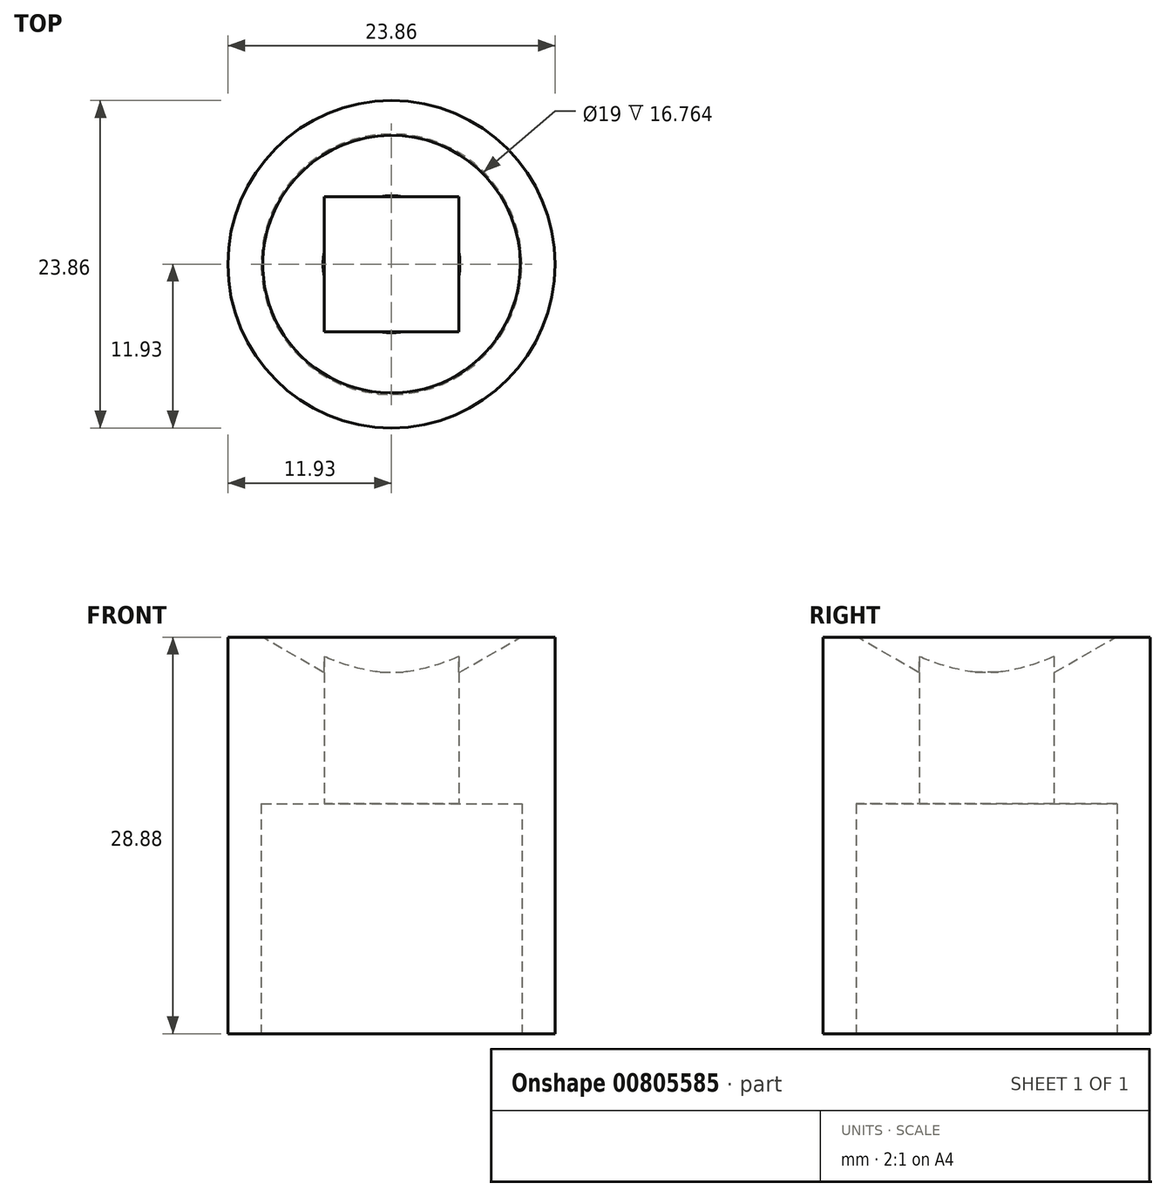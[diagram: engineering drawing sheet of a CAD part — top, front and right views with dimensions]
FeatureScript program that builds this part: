
annotation { "Feature Type Name" : "Feature", "Feature Type Description" : "" }
export const myFeature = defineFeature(function(context is Context, id is Id, definition is map)
    precondition{}
    {
        {
            var Q0;
            Q0=qCreatedBy(makeId("Top.planeOp"),FACE);
            var sketch = newSketch(context, id + "F0", { "sketchPlane" : qUnion([Q0])});
            skCircle(sketch, "E0", {"center": v(0, 0) * mm, "radius": 11.93 * mm});
            skSolve(sketch);
        }
        {
            var Q0;
            Q0 = qSketchRegion(id + "F0", true);
            extrude(context, id + "F1", {"entities" : qUnion([Q0]), "depth" : 28.88 * mm, "offsetDistance" : 25.4 * mm});
        }
        {
            var Q0;
            Q0=makeQuery(id+"F1.opExtrude","CAP_FACE",FACE,{"disambiguationData":[OSD([sQuery(id+"F0.wireOp",EDGE,"E0")])],"isStart":false});
            var sketch = newSketch(context, id + "F2", { "sketchPlane" : qUnion([Q0])});
            skCircle(sketch, "E1.0", {"center": v(0, 0) * mm, "radius": 9.39 * mm});
            skSolve(sketch);
        }
        {
            var Q0;
            Q0=makeQuery(id+"F2.imprint","IMPRINT",FACE,{"disambiguationData":[TD([[makeQuery(id+"F2.imprint","IMPRINT",EDGE,{"derivedFrom":sQuery(id+"F2.wireOp",EDGE,"E1.0")}),1.0]])]});
            var Q1;
            Q1=sQuery(id+"F2.wireOp",EDGE,"E1.0");
            extrude(context, id + "F3", {"entities" : qUnion([Q0]), "operationType" : NewBodyOperationType.REMOVE, "surfaceEntities" : qUnion([Q1]), "oppositeDirection" : true, "depth" : 2.54 * mm, "offsetDistance" : 25.4 * mm, "hasDraft" : true, "draftAngle" : 60 * degree, "draftPullDirection" : true});
        }
        {
            var Q0;
            Q0=makeQuery(id+"F1.opExtrude","CAP_FACE",FACE,{"disambiguationData":[OSD([sQuery(id+"F0.wireOp",EDGE,"E0")])],"isStart":true});
            var sketch = newSketch(context, id + "F4", { "sketchPlane" : qUnion([Q0])});
            skCircle(sketch, "E2.0", {"center": v(0, 0) * mm, "radius": 9.5 * mm});
            skSolve(sketch);
        }
        {
            var Q0;
            Q0 = qSketchRegion(id + "F4", true);
            extrude(context, id + "F5", {"entities" : qUnion([Q0]), "operationType" : NewBodyOperationType.REMOVE, "oppositeDirection" : true, "depth" : 16.76 * mm, "offsetDistance" : 25.4 * mm});
        }
        {
            var Q0;
            Q0=makeQuery(id+"F5.boolean.opBoolean","COPY",FACE,{"derivedFrom":makeQuery(id+"F5.opExtrude","CAP_FACE",FACE,{"disambiguationData":[OSD([sQuery(id+"F4.wireOp",EDGE,"E2.0")])],"isStart":false})});
            var sketch = newSketch(context, id + "F6", { "sketchPlane" : qUnion([Q0])});
            skLineSegment(sketch, "E3.bottom", {"start": v(4.91, -4.91) * mm, "end": v(-4.91, -4.91) * mm});
            skLineSegment(sketch, "E3.top", {"start": v(4.91, 4.91) * mm, "end": v(-4.91, 4.91) * mm});
            skLineSegment(sketch, "E3.left", {"start": v(4.91, -4.91) * mm, "end": v(4.91, 4.91) * mm});
            skLineSegment(sketch, "E3.right", {"start": v(-4.91, -4.91) * mm, "end": v(-4.91, 4.91) * mm});
            skPoint(sketch, "E3.middle", {"position": v(0, 0) * mm});
            skSolve(sketch);
        }
        {
            var Q0;
            Q0 = qSketchRegion(id + "F6", true);
            extrude(context, id + "F7", {"entities" : qUnion([Q0]), "operationType" : NewBodyOperationType.REMOVE, "endBound" : BoundingType.THROUGH_ALL, "oppositeDirection" : true, "depth" : 25.4 * mm, "offsetDistance" : 25.4 * mm});
        }
    });
